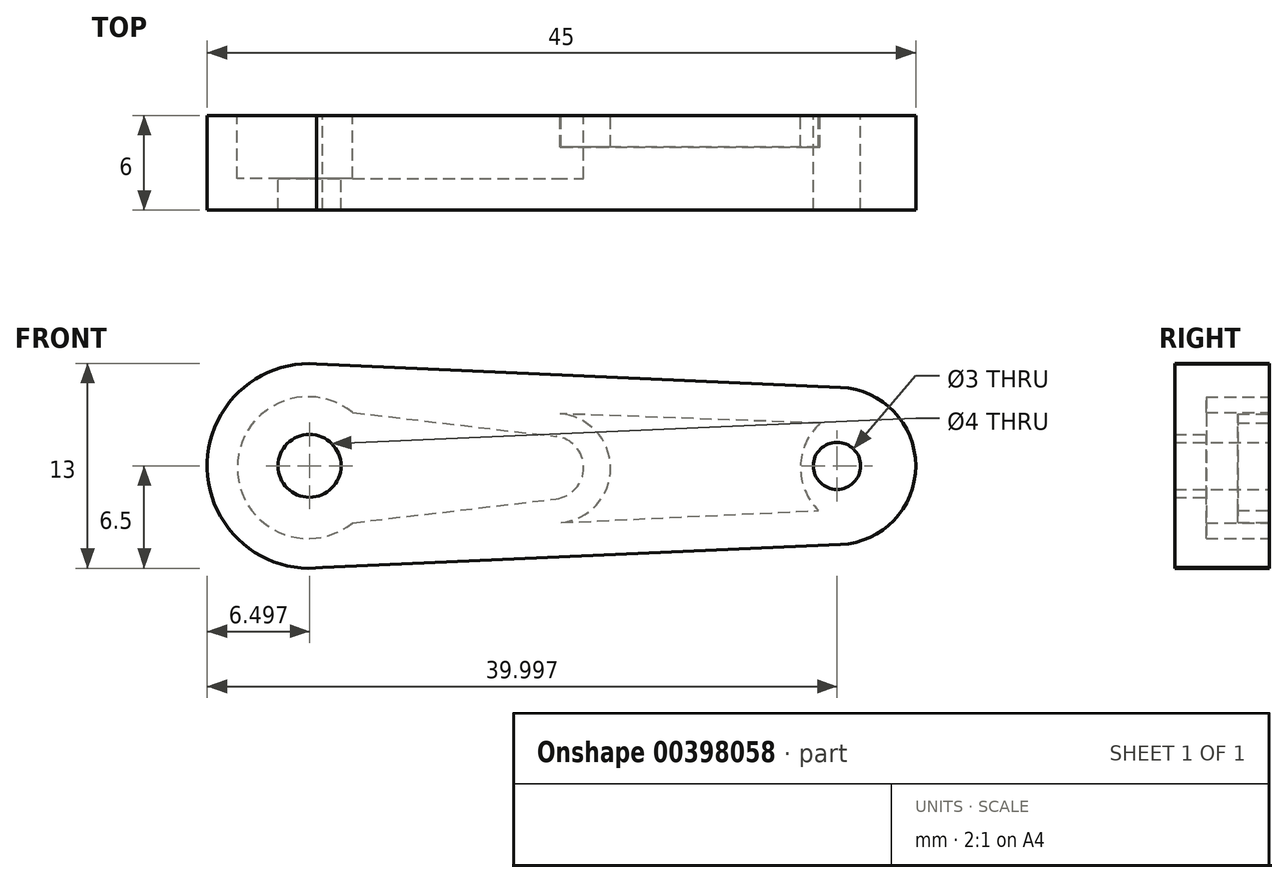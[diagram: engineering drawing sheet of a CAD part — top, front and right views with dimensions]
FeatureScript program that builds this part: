
annotation { "Feature Type Name" : "Feature", "Feature Type Description" : "" }
export const myFeature = defineFeature(function(context is Context, id is Id, definition is map)
    precondition{}
    {
        {
            var Q0;
            Q0=qCreatedBy(makeId("Front.planeOp"),FACE);
            var sketch = newSketch(context, id + "F0", { "sketchPlane" : qUnion([Q0])});
            skCircle(sketch, "E0", {"center": v(0.09, 0.1) * mm, "radius": 6.5 * mm});
            skCircle(sketch, "E1", {"center": v(33.59, 0.1) * mm, "radius": 5 * mm});
            skLineSegment(sketch, "E2", {"start": v(0.23, 6.6) * mm, "end": v(33.81, 5.1) * mm});
            skLineSegment(sketch, "E3", {"start": v(-0.18, -6.38) * mm, "end": v(33.8, -4.89) * mm});
            skLineSegment(sketch, "E4", {"start": v(-6.41, 0.1) * mm, "end": v(38.59, 0.1) * mm});
            skCircle(sketch, "E5", {"center": v(0.09, 0.1) * mm, "radius": 2 * mm});
            skCircle(sketch, "E6", {"center": v(33.59, 0.1) * mm, "radius": 1.5 * mm});
            skSolve(sketch);
        }
        {
            var Q0;
            Q0 = qSketchRegion(id + "F0", true);
            extrude(context, id + "F1", {"entities" : qUnion([Q0]), "depth" : 6 * mm});
        }
        {
            var Q0;
            Q0=qCreatedBy(makeId("Front.planeOp"),FACE);
            var sketch = newSketch(context, id + "F2", { "sketchPlane" : qUnion([Q0])});
            skCircle(sketch, "E7", {"center": v(0, 0) * mm, "radius": 4.5 * mm});
            skLineSegment(sketch, "E8", {"start": v(-4.5, 0) * mm, "end": v(15.5, 0) * mm});
            skCircle(sketch, "E9", {"center": v(15.5, 0) * mm, "radius": 2 * mm});
            skLineSegment(sketch, "E10", {"start": v(0, -4.5) * mm, "end": v(0, 4.5) * mm});
            skLineSegment(sketch, "E11", {"start": v(0, 4.5) * mm, "end": v(0, -4.5) * mm});
            skLineSegment(sketch, "E12", {"start": v(2.82, -3.5) * mm, "end": v(15.73, -1.99) * mm});
            skLineSegment(sketch, "E13", {"start": v(15.73, -1.99) * mm, "end": v(2.82, -3.5) * mm});
            skLineSegment(sketch, "E14", {"start": v(2.82, -3.5) * mm, "end": v(2.82, 3.5) * mm});
            skLineSegment(sketch, "E15", {"start": v(2.82, 3.5) * mm, "end": v(15.73, 1.99) * mm});
            skSolve(sketch);
        }
        {
            var Q0;
            Q0 = qSketchRegion(id + "F2", true);
            extrude(context, id + "F3", {"entities" : qUnion([Q0]), "operationType" : NewBodyOperationType.REMOVE, "depth" : 4 * mm});
        }
        {
            var Q0;
            Q0=makeQuery(id+"F1.opExtrude","CAP_FACE",FACE,{"disambiguationData":[OSD([sQuery(id+"F0.wireOp",EDGE,"E0"),sQuery(id+"F0.wireOp",EDGE,"E1"),sQuery(id+"F0.wireOp",EDGE,"E2"),sQuery(id+"F0.wireOp",EDGE,"E3"),sQuery(id+"F0.wireOp",EDGE,"E5"),sQuery(id+"F0.wireOp",EDGE,"E6")])],"isStart":true});
            var sketch = newSketch(context, id + "F4", { "sketchPlane" : qUnion([Q0])});
            skArc(sketch, "E16", {"start": v(-15.73, 3.43) * mm, "mid": v(-19.2, -0.04) * mm, "end": v(-15.73, -3.51) * mm});
            skArc(sketch, "E17", {"start": v(-32.42, -2.73) * mm, "mid": v(-31.27, 0.07) * mm, "end": v(-32.52, 2.82) * mm});
            skLineSegment(sketch, "E18", {"start": v(-32.52, 2.82) * mm, "end": v(-15.73, 3.43) * mm});
            skLineSegment(sketch, "E19", {"start": v(-15.73, -3.51) * mm, "end": v(-32.42, -2.73) * mm});
            skSolve(sketch);
        }
        {
            var Q0;
            {var subQ5=sQuery(id+"F4.wireOp",EDGE,"E17");Q0=makeQuery(id+"F4.imprint","IMPRINT",FACE,{"disambiguationData":[TD([[makeQuery(id+"F4.imprint","IMPRINT",EDGE,{"derivedFrom":subQ5}),-1.0]])]});}
            extrude(context, id + "F5", {"entities" : qUnion([Q0]), "operationType" : NewBodyOperationType.REMOVE, "oppositeDirection" : true, "depth" : 2 * mm});
        }
    });
